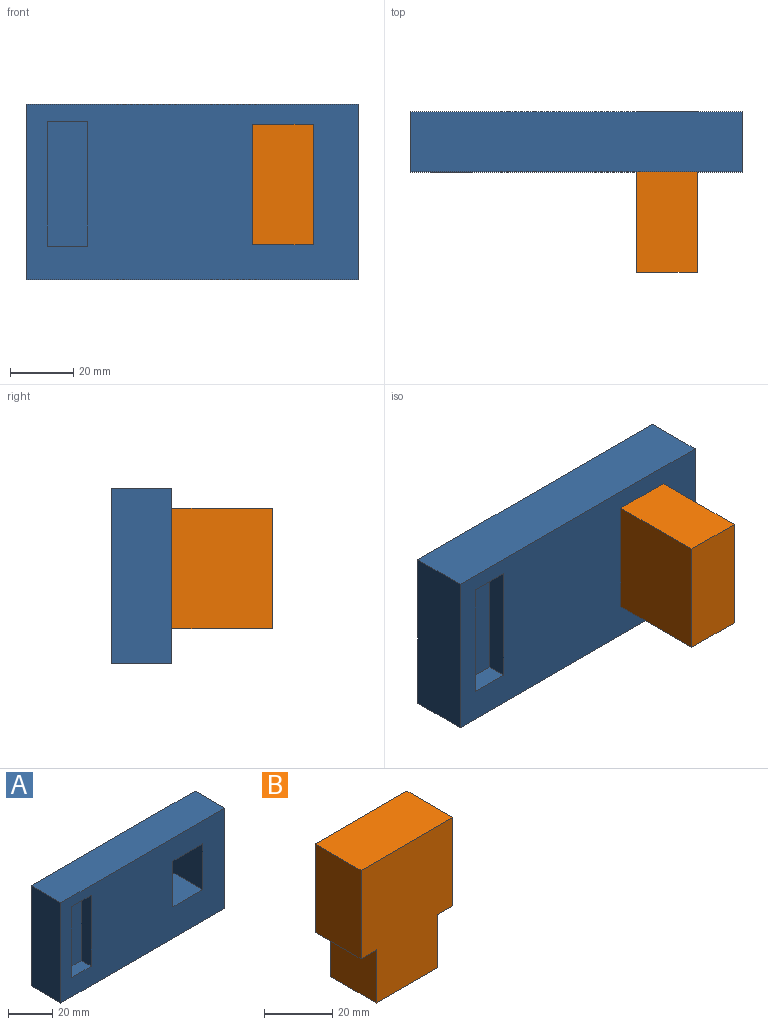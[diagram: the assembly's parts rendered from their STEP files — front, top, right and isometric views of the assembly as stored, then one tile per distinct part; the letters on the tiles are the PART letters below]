
ASSEMBLY  parts=2 mates=1
PART A: 15 faces, bbox 105x19.1x55.6 mm
  f0: plane 105.05x55.57mm, normal (0,-1,0), area 4853.9mm2, adj f1,f2,f3,f4,f6,f7,f8,f9
  f1: plane 105.05x19.05mm, normal (0,0,1), area 2001.2mm2, adj f0,f2,f4,f5
  f2: plane 55.57x19.05mm, normal (-1,0,0), area 1058.6mm2, adj f0,f1,f3,f5
  f3: plane 105.05x19.05mm, normal (0,0,-1), area 2001.2mm2, adj f0,f2,f4,f5
  f4: plane 55.57x19.05mm, normal (1,0,0), area 1058.6mm2, adj f0,f1,f3,f5
  f5: plane 105.05x55.57mm, normal (0,1,0), area 5353.9mm2, adj f1,f2,f3,f4,f6,f7,f8,f9
  f6: plane 25.4x19.05mm, normal (1,0,0), area 483.9mm2, adj f0,f5,f7,f9
  f7: plane 19.05x19.05mm, normal (0,0,1), area 362.9mm2, adj f0,f5,f6,f8
  f8: plane 25.4x19.05mm, normal (-1,0,0), area 483.9mm2, adj f0,f5,f7,f9
  f9: plane 19.05x19.05mm, normal (0,0,-1), area 362.9mm2, adj f0,f5,f6,f8
  f10: plane 39.37x6.35mm, normal (-1,0,0), area 250mm2, adj f0,f11,f13,f14
  f11: plane 12.7x6.35mm, normal (0,0,-1), area 80.6mm2, adj f0,f10,f12,f14
  f12: plane 39.37x6.35mm, normal (1,0,0), area 250mm2, adj f0,f11,f13,f14
  f13: plane 12.7x6.35mm, normal (0,0,1), area 80.6mm2, adj f0,f10,f12,f14
  f14: plane 39.37x12.7mm, normal (0,-1,0), area 500mm2, adj f10,f11,f12,f13
PART B: 10 faces, bbox 38.1x19.1x50.8 mm
  f0: plane 19.05x6.35mm, normal (0,0,-1), area 121mm2, adj f1,f7,f8,f9
  f1: plane 19.05x19.05mm, normal (-1,0,0), area 362.9mm2, adj f0,f2,f8,f9
  f2: plane 25.4x19.05mm, normal (0,0,-1), area 483.9mm2, adj f1,f3,f8,f9
  f3: plane 19.05x19.05mm, normal (1,0,0), area 362.9mm2, adj f2,f4,f8,f9
  f4: plane 19.05x6.35mm, normal (0,0,-1), area 121mm2, adj f3,f5,f8,f9
  f5: plane 31.75x19.05mm, normal (1,0,0), area 604.8mm2, adj f4,f6,f8,f9
  f6: plane 38.1x19.05mm, normal (0,0,1), area 725.8mm2, adj f5,f7,f8,f9
  f7: plane 31.75x19.05mm, normal (-1,0,0), area 604.8mm2, adj f0,f6,f8,f9
  f8: plane 50.8x38.1mm, normal (0,-1,0), area 1693.5mm2, adj f0,f1,f2,f3,f4,f5,f6,f7
  f9: plane 50.8x38.1mm, normal (0,1,0), area 1693.5mm2, adj f0,f1,f2,f3,f4,f5,f6,f7
PLACE A t=(-10.38,30.21,24)mm
PLACE B rot(axis=(0.58,0.58,-0.58),120deg) t=(17.42,28.96,-1.08)mm
MATE fastened B.f2 <-> A.f5  axis (0,-1,0) through (17.42,30.21,66.87)mm
